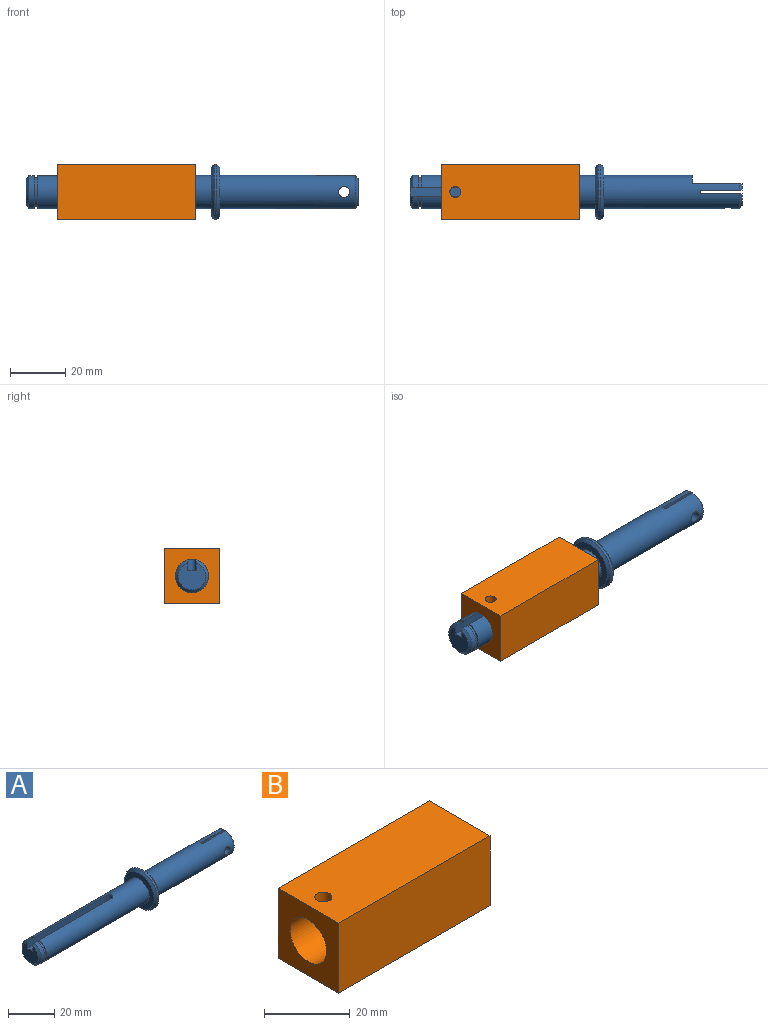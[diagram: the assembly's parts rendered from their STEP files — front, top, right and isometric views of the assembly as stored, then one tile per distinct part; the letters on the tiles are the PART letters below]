
ASSEMBLY  parts=2 mates=1
PART A: 29 faces, bbox 120.1x20.1x20.1 mm
  f0: cylinder r=6mm len=62.8mm, axis (-1,0,0), area 2229.6mm2, adj f5,f22,f23,f25,f28
  f1: cylinder r=6mm len=12mm, axis (-1,0,0), area 69.3mm2, adj f3,f22,f23,f26
  f2: plane 10x9.77mm, normal (-1,0,0), area 69.8mm2, adj f3,f22,f23,f24
  f3: cone r=6mm half-angle=45deg, axis (1,0,0), area 44.5mm2, adj f1,f2,f22,f23
  f4: cylinder r=10mm len=20mm, axis (1,0,0), area 62.8mm2, adj f20,f21
  f5: plane 18x18mm, normal (-1,0,0), area 141.4mm2, adj f0,f20
  f6: plane 18x18mm, normal (1,0,0), area 141.4mm2, adj f19,f21
  f7: plane 9.93x4.4mm, normal (1,0,0), area 33.3mm2, adj f12,f13
  f8: plane 9.93x2.4mm, normal (1,0,0), area 22.1mm2, adj f11,f15,f16,f17
  f9: cylinder r=2mm len=4mm, axis (0,1,0), area 30.2mm2, adj f15,f17
  f10: plane 10.39x3mm, normal (1,0,0), area 22.1mm2, adj f17,f19
  f11: cone r=5mm half-angle=45deg, axis (-1,0,0), area 3.7mm2, adj f8,f15,f17,f19
  f12: cone r=5mm half-angle=45deg, axis (-1,0,0), area 22.7mm2, adj f7,f13,f19
  f13: plane 15.01x11.95mm, normal (0,1,0), area 165.5mm2, adj f7,f12,f14,f18,f19
  f14: plane 12x1.2mm, normal (1,0,0), area 14.4mm2, adj f13,f15,f19
  f15: plane 15.01x11.95mm, normal (0,-1,0), area 165.5mm2, adj f8,f9,f11,f14,f16,f19
  f16: cone r=5mm half-angle=45deg, axis (-1,0,0), area 3.7mm2, adj f8,f15,f17,f19
  f17: plane 18.07x10.46mm, normal (0,1,0), area 173.3mm2, adj f8,f9,f10,f11,f16,f19
  f18: cylinder r=2mm len=5.4mm, axis (0,1,0), area 65.7mm2, adj f13,f19
  f19: cylinder r=6mm len=49mm, axis (-1,0,0), area 1587.3mm2, adj f6,f10,f11,f12,f13,f14,f15,f16
  f20: cone r=10mm half-angle=45deg, axis (1,0,0), area 84.4mm2, adj f4,f5
  f21: cone r=9mm half-angle=45deg, axis (-1,0,0), area 84.4mm2, adj f4,f6
  f22: plane 48.53x3.84mm, normal (0,-1,0), area 183.5mm2, adj f0,f1,f2,f3,f24,f25,f26,f27
  f23: plane 48.53x3.84mm, normal (0,1,0), area 183.5mm2, adj f0,f1,f2,f3,f24,f25,f26,f27
  f24: plane 50x3mm, normal (0,0,1), area 149mm2, adj f2,f22,f23,f25
  f25: cylinder r=1.5mm len=4mm, axis (0,0,-1), area 18.4mm2, adj f0,f22,f23,f24
  f26: plane 12x11.81mm, normal (1,0,0), area 19.7mm2, adj f1,f22,f23,f27
  f27: cylinder r=5.4mm len=10.8mm, axis (1,0,0), area 37.1mm2, adj f22,f23,f26,f28
  f28: plane 12x11.81mm, normal (-1,0,0), area 19.7mm2, adj f0,f22,f23,f27
PART B: 10 faces, bbox 50x20x20 mm
  f0: cylinder r=6mm len=20mm, axis (-1,0,0), area 741.2mm2, adj f6,f8,f9
  f1: plane 50x20mm, normal (0,-1,0), area 1000mm2, adj f2,f4,f5,f6
  f2: plane 50x20mm, normal (0,0,-1), area 1000mm2, adj f1,f3,f5,f6
  f3: plane 50x20mm, normal (0,1,0), area 1000mm2, adj f2,f4,f5,f6
  f4: plane 50x20mm, normal (0,0,1), area 987.4mm2, adj f1,f3,f5,f6,f9
  f5: plane 20x20mm, normal (1,0,0), area 145.5mm2, adj f1,f2,f3,f4,f7
  f6: plane 20x20mm, normal (-1,0,0), area 286.9mm2, adj f0,f1,f2,f3,f4
  f7: cylinder r=9mm len=30mm, axis (1,0,0), area 1696.5mm2, adj f5,f8
  f8: plane 18x18mm, normal (1,0,0), area 141.4mm2, adj f0,f7
  f9: cylinder r=2mm len=4.34mm, axis (0,0,1), area 52.4mm2, adj f0,f4
PLACE A t=(29.66,16.87,110.61)mm
PLACE B t=(41.05,16.87,110.61)mm
MATE slider A.f0 <-> B.f7  axis (-1,0,0) through (29.66,16.87,110.61)mm
